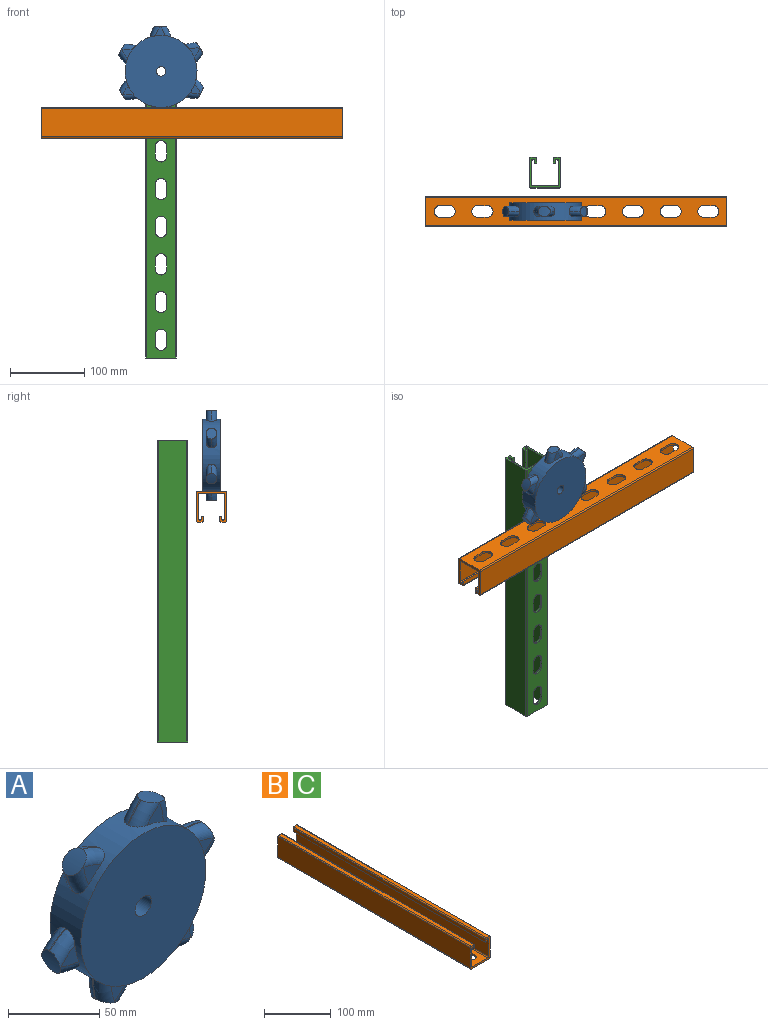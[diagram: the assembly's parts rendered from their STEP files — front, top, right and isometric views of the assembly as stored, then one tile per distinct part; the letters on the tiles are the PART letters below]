
ASSEMBLY  parts=3 mates=2
PART A: 58 faces, bbox 135.5x23.8x134.3 mm
  f0: cylinder r=48.5mm len=97.01mm, axis (0,1,0), area 5084.7mm2, adj f2,f3,f4,f5,f7,f8,f9,f10
  f1: cylinder r=6.35mm len=23.81mm, axis (0,1,0), area 950.1mm2, adj f2,f3
  f2: plane 97.01x97.01mm, normal (0,-1,0), area 7264.3mm2, adj f0,f1
  f3: plane 97.01x97.01mm, normal (0,1,0), area 7264.3mm2, adj f0,f1
  f4: cylinder r=48.5mm len=15.18mm, axis (0,1,0), area 8.8mm2, adj f0,f6,f9,f11
  f5: cylinder r=48.5mm len=12.54mm, axis (0,1,0), area 8.8mm2, adj f0,f6,f10,f12
  f6: cylinder r=61.2mm len=16.09mm, axis (0,1,0), area 185mm2, adj f4,f5,f9,f10,f11,f12
  f7: plane 13.69x12.69mm, normal (0,-1,0), area 89.3mm2, adj f0,f11,f12
  f8: plane 13.69x12.69mm, normal (0,1,0), area 89.3mm2, adj f0,f9,f10
  f9: torus R=41.65mm, axis (0,-1,0), area 164.2mm2, adj f0,f4,f6,f8,f10
  f10: torus R=41.65mm, axis (0,-1,0), area 164.2mm2, adj f0,f5,f6,f8,f9
  f11: torus R=41.65mm, axis (0,-1,0), area 164.2mm2, adj f0,f4,f6,f7,f12
  f12: torus R=41.65mm, axis (0,-1,0), area 164.2mm2, adj f0,f5,f6,f7,f11
  f13: cylinder r=48.5mm len=14.36mm, axis (0,1,0), area 8.8mm2, adj f0,f15,f18,f20
  f14: cylinder r=48.5mm len=13.97mm, axis (0,1,0), area 8.8mm2, adj f0,f15,f19,f21
  f15: cylinder r=61.2mm len=14.27mm, axis (0,1,0), area 185mm2, adj f13,f14,f18,f19,f20,f21
  f16: plane 13.61x13.33mm, normal (0,-1,0), area 89.3mm2, adj f0,f20,f21
  f17: plane 13.61x13.33mm, normal (0,1,0), area 89.3mm2, adj f0,f18,f19
  f18: torus R=41.65mm, axis (0,-1,0), area 164.2mm2, adj f0,f13,f15,f17,f19
  f19: torus R=41.65mm, axis (0,-1,0), area 164.2mm2, adj f0,f14,f15,f17,f18
  f20: torus R=41.65mm, axis (0,-1,0), area 164.2mm2, adj f0,f13,f15,f16,f21
  f21: torus R=41.65mm, axis (0,-1,0), area 164.2mm2, adj f0,f14,f15,f16,f20
  f22: cylinder r=48.5mm len=11.93mm, axis (0,1,0), area 8.8mm2, adj f0,f24,f27,f29
  f23: cylinder r=48.5mm len=15.31mm, axis (0,1,0), area 8.8mm2, adj f0,f24,f28,f30
  f24: cylinder r=61.2mm len=15.81mm, axis (0,1,0), area 185mm2, adj f22,f23,f27,f28,f29,f30
  f25: plane 13.89x12.47mm, normal (0,-1,0), area 89.3mm2, adj f0,f29,f30
  f26: plane 13.89x12.47mm, normal (0,1,0), area 89.3mm2, adj f0,f27,f28
  f27: torus R=41.65mm, axis (0,-1,0), area 164.2mm2, adj f0,f22,f24,f26,f28
  f28: torus R=41.65mm, axis (0,-1,0), area 164.2mm2, adj f0,f23,f24,f26,f27
  f29: torus R=41.65mm, axis (0,-1,0), area 164.2mm2, adj f0,f22,f24,f25,f30
  f30: torus R=41.65mm, axis (0,-1,0), area 164.2mm2, adj f0,f23,f24,f25,f29
  f31: cylinder r=48.5mm len=15.18mm, axis (0,1,0), area 8.8mm2, adj f0,f33,f36,f38
  f32: cylinder r=48.5mm len=12.54mm, axis (0,1,0), area 8.8mm2, adj f0,f33,f37,f39
  f33: cylinder r=61.2mm len=16.09mm, axis (0,1,0), area 185mm2, adj f31,f32,f36,f37,f38,f39
  f34: plane 13.69x12.69mm, normal (0,-1,0), area 89.3mm2, adj f0,f38,f39
  f35: plane 13.69x12.69mm, normal (0,1,0), area 89.3mm2, adj f0,f36,f37
  f36: torus R=41.65mm, axis (0,-1,0), area 164.2mm2, adj f0,f31,f33,f35,f37
  f37: torus R=41.65mm, axis (0,-1,0), area 164.2mm2, adj f0,f32,f33,f35,f36
  f38: torus R=41.65mm, axis (0,-1,0), area 164.2mm2, adj f0,f31,f33,f34,f39
  f39: torus R=41.65mm, axis (0,-1,0), area 164.2mm2, adj f0,f32,f33,f34,f38
  f40: cylinder r=48.5mm len=14.36mm, axis (0,1,0), area 8.8mm2, adj f0,f42,f45,f47
  f41: cylinder r=48.5mm len=13.97mm, axis (0,1,0), area 8.8mm2, adj f0,f42,f46,f48
  f42: cylinder r=61.2mm len=14.27mm, axis (0,1,0), area 185mm2, adj f40,f41,f45,f46,f47,f48
  f43: plane 13.61x13.33mm, normal (0,-1,0), area 89.3mm2, adj f0,f47,f48
  f44: plane 13.61x13.33mm, normal (0,1,0), area 89.3mm2, adj f0,f45,f46
  f45: torus R=41.65mm, axis (0,-1,0), area 164.2mm2, adj f0,f40,f42,f44,f46
  f46: torus R=41.65mm, axis (0,-1,0), area 164.2mm2, adj f0,f41,f42,f44,f45
  f47: torus R=41.65mm, axis (0,-1,0), area 164.2mm2, adj f0,f40,f42,f43,f48
  f48: torus R=41.65mm, axis (0,-1,0), area 164.2mm2, adj f0,f41,f42,f43,f47
  f49: cylinder r=48.5mm len=15.31mm, axis (0,1,0), area 8.8mm2, adj f0,f50,f55,f57
  f50: cylinder r=61.2mm len=15.81mm, axis (0,1,0), area 185mm2, adj f49,f51,f54,f55,f56,f57
  f51: cylinder r=48.5mm len=11.93mm, axis (0,1,0), area 8.8mm2, adj f0,f50,f54,f56
  f52: plane 13.89x12.47mm, normal (0,-1,0), area 89.3mm2, adj f0,f56,f57
  f53: plane 13.89x12.47mm, normal (0,1,0), area 89.3mm2, adj f0,f54,f55
  f54: torus R=41.65mm, axis (0,-1,0), area 164.2mm2, adj f0,f50,f51,f53,f55
  f55: torus R=41.65mm, axis (0,-1,0), area 164.2mm2, adj f0,f49,f50,f53,f54
  f56: torus R=41.65mm, axis (0,-1,0), area 164.2mm2, adj f0,f50,f51,f52,f57
  f57: torus R=41.65mm, axis (0,-1,0), area 164.2mm2, adj f0,f49,f50,f52,f56
PART B: 62 faces, bbox 41.3x406.4x41.3 mm
  f0: plane 406.4x38.1mm, normal (0,0,-1), area 12287.5mm2, adj f3,f4,f28,f29,f30,f31,f32,f33
  f1: plane 406.4x32.54mm, normal (0,0,1), area 10029.4mm2, adj f16,f17,f28,f29,f30,f31,f32,f33
  f2: plane 406.4x38.1mm, normal (-1,0,0), area 15483.8mm2, adj f3,f27,f28,f29
  f3: cylinder r=1.59mm len=406.4mm, axis (0,-1,0), area 1013.4mm2, adj f0,f2,f28,f29
  f4: cylinder r=1.59mm len=406.4mm, axis (0,-1,0), area 1013.4mm2, adj f0,f5,f28,f29
  f5: plane 406.4x38.1mm, normal (1,0,0), area 15483.8mm2, adj f4,f6,f28,f29
  f6: cylinder r=1.59mm len=406.4mm, axis (0,-1,0), area 1013.4mm2, adj f5,f7,f28,f29
  f7: plane 406.4x6.35mm, normal (0,0,1), area 2580.6mm2, adj f6,f8,f28,f29
  f8: cylinder r=1.59mm len=406.4mm, axis (0,-1,0), area 1013.4mm2, adj f7,f9,f28,f29
  f9: plane 406.4x6.35mm, normal (-1,0,0), area 2580.6mm2, adj f8,f10,f28,f29
  f10: plane 406.4x2.78mm, normal (0,0,-1), area 1129mm2, adj f9,f11,f28,f29
  f11: plane 406.4x3.57mm, normal (1,0,0), area 1451.6mm2, adj f10,f12,f28,f29
  f12: cylinder r=1.59mm len=406.4mm, axis (0,-1,0), area 1013.4mm2, adj f11,f13,f28,f29
  f13: plane 406.4x0.79mm, normal (0,0,-1), area 322.6mm2, adj f12,f14,f28,f29
  f14: cylinder r=1.59mm len=406.4mm, axis (0,-1,0), area 1013.4mm2, adj f13,f15,f28,f29
  f15: plane 406.4x32.54mm, normal (-1,0,0), area 13225.8mm2, adj f14,f16,f28,f29
  f16: cylinder r=1.59mm len=406.4mm, axis (0,-1,0), area 1013.4mm2, adj f1,f15,f28,f29
  f17: cylinder r=1.59mm len=406.4mm, axis (0,-1,0), area 1013.4mm2, adj f1,f18,f28,f29
  f18: plane 406.4x32.54mm, normal (1,0,0), area 13225.8mm2, adj f17,f19,f28,f29
  f19: cylinder r=1.59mm len=406.4mm, axis (0,-1,0), area 1013.4mm2, adj f18,f20,f28,f29
  f20: plane 406.4x0.79mm, normal (0,0,-1), area 322.6mm2, adj f19,f21,f28,f29
  f21: cylinder r=1.59mm len=406.4mm, axis (0,-1,0), area 1013.4mm2, adj f20,f22,f28,f29
  f22: plane 406.4x3.57mm, normal (-1,0,0), area 1451.6mm2, adj f21,f23,f28,f29
  f23: plane 406.4x2.78mm, normal (0,0,-1), area 1129mm2, adj f22,f24,f28,f29
  f24: plane 406.4x6.35mm, normal (1,0,0), area 2580.6mm2, adj f23,f25,f28,f29
  f25: cylinder r=1.59mm len=406.4mm, axis (0,-1,0), area 1013.4mm2, adj f24,f26,f28,f29
  f26: plane 406.4x6.35mm, normal (0,0,1), area 2580.6mm2, adj f25,f27,f28,f29
  f27: cylinder r=1.59mm len=406.4mm, axis (0,-1,0), area 1013.4mm2, adj f2,f26,f28,f29
  f28: plane 41.28x41.28mm, normal (0,1,0), area 394.7mm2, adj f0,f1,f2,f3,f4,f5,f6,f7
  f29: plane 41.28x41.28mm, normal (0,-1,0), area 394.7mm2, adj f0,f1,f2,f3,f4,f5,f6,f7
  f30: plane 12.7x2.78mm, normal (-1,0,0), area 35.3mm2, adj f0,f1,f31,f33
  f31: cylinder r=7.94mm len=15.88mm, axis (0,0,1), area 69.3mm2, adj f0,f1,f30,f32
  f32: plane 12.7x2.78mm, normal (1,0,0), area 35.3mm2, adj f0,f1,f31,f33
  f33: cylinder r=7.94mm len=15.88mm, axis (0,0,1), area 69.3mm2, adj f0,f1,f30,f32
  f34: plane 12.7x2.78mm, normal (-1,0,0), area 35.3mm2, adj f0,f1,f35,f37
  f35: cylinder r=7.94mm len=15.88mm, axis (0,0,1), area 69.3mm2, adj f0,f1,f34,f36
  f36: plane 12.7x2.78mm, normal (1,0,0), area 35.3mm2, adj f0,f1,f35,f37
  f37: cylinder r=7.94mm len=15.88mm, axis (0,0,1), area 69.3mm2, adj f0,f1,f34,f36
  f38: plane 12.7x2.78mm, normal (-1,0,0), area 35.3mm2, adj f0,f1,f39,f41
  f39: cylinder r=7.94mm len=15.88mm, axis (0,0,1), area 69.3mm2, adj f0,f1,f38,f40
  f40: plane 12.7x2.78mm, normal (1,0,0), area 35.3mm2, adj f0,f1,f39,f41
  f41: cylinder r=7.94mm len=15.88mm, axis (0,0,1), area 69.3mm2, adj f0,f1,f38,f40
  f42: plane 12.7x2.78mm, normal (-1,0,0), area 35.3mm2, adj f0,f1,f43,f45
  f43: cylinder r=7.94mm len=15.88mm, axis (0,0,1), area 69.3mm2, adj f0,f1,f42,f44
  f44: plane 12.7x2.78mm, normal (1,0,0), area 35.3mm2, adj f0,f1,f43,f45
  f45: cylinder r=7.94mm len=15.88mm, axis (0,0,1), area 69.3mm2, adj f0,f1,f42,f44
  f46: plane 12.7x2.78mm, normal (-1,0,0), area 35.3mm2, adj f0,f1,f47,f49
  f47: cylinder r=7.94mm len=15.88mm, axis (0,0,1), area 69.3mm2, adj f0,f1,f46,f48
  f48: plane 12.7x2.78mm, normal (1,0,0), area 35.3mm2, adj f0,f1,f47,f49
  f49: cylinder r=7.94mm len=15.88mm, axis (0,0,1), area 69.3mm2, adj f0,f1,f46,f48
  f50: plane 12.7x2.78mm, normal (-1,0,0), area 35.3mm2, adj f0,f1,f51,f53
  f51: cylinder r=7.94mm len=15.88mm, axis (0,0,1), area 69.3mm2, adj f0,f1,f50,f52
  f52: plane 12.7x2.78mm, normal (1,0,0), area 35.3mm2, adj f0,f1,f51,f53
  f53: cylinder r=7.94mm len=15.88mm, axis (0,0,1), area 69.3mm2, adj f0,f1,f50,f52
  f54: plane 12.7x2.78mm, normal (-1,0,0), area 35.3mm2, adj f0,f1,f55,f57
  f55: cylinder r=7.94mm len=15.88mm, axis (0,0,1), area 69.3mm2, adj f0,f1,f54,f56
  f56: plane 12.7x2.78mm, normal (1,0,0), area 35.3mm2, adj f0,f1,f55,f57
  f57: cylinder r=7.94mm len=15.88mm, axis (0,0,1), area 69.3mm2, adj f0,f1,f54,f56
  f58: cylinder r=7.94mm len=15.88mm, axis (0,0,1), area 69.3mm2, adj f0,f1,f59,f61
  f59: plane 12.7x2.78mm, normal (1,0,0), area 35.3mm2, adj f0,f1,f58,f60
  f60: cylinder r=7.94mm len=15.88mm, axis (0,0,1), area 69.3mm2, adj f0,f1,f59,f61
  f61: plane 12.7x2.78mm, normal (-1,0,0), area 35.3mm2, adj f0,f1,f58,f60
PART C: same geometry as B
PLACE A rot(axis=(0,1,0),41.9deg) t=(-41.51,7.1,48.68)mm
PLACE B rot(axis=(0.71,0.71,0),180deg) t=(-203,0,-20.64)mm
PLACE C rot(axis=(-1,0,0),90deg) t=(-41.51,52.5,68.5)mm
MATE revolute A.f0 <-> C.f60  axis (0,1,0) through (-41.51,11.86,48.68)mm
MATE slider C.f5 <-> B.f28  axis (1,0,0) through (-20.87,52.5,68.5)mm
